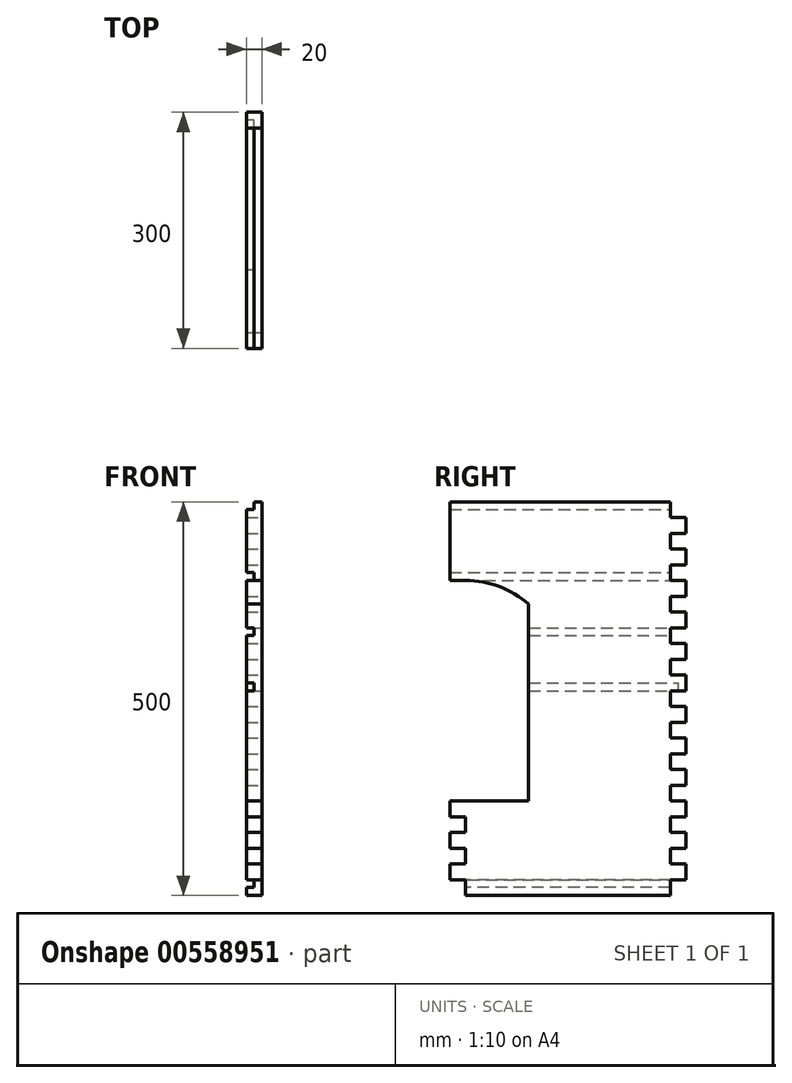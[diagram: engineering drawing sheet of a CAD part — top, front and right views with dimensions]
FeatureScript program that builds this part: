
annotation { "Feature Type Name" : "Feature", "Feature Type Description" : "" }
export const myFeature = defineFeature(function(context is Context, id is Id, definition is map)
    precondition{}
    {
        {
            var Q0;
            Q0=qCreatedBy(makeId("Right.planeOp"),FACE);
            var sketch = newSketch(context, id + "F0", { "sketchPlane" : qUnion([Q0])});
            skLineSegment(sketch, "E0.bottom", {"start": v(150, -250) * mm, "end": v(-150, -250) * mm});
            skLineSegment(sketch, "E0.left", {"start": v(150, -250) * mm, "end": v(150, 250) * mm});
            skPoint(sketch, "E0.middle", {"position": v(0, 0) * mm});
            skLineSegment(sketch, "E1", {"start": v(-150, -250) * mm, "end": v(-150, -130) * mm});
            skLineSegment(sketch, "E2", {"start": v(150, 250) * mm, "end": v(-50, 250) * mm});
            skLineSegment(sketch, "E3", {"start": v(-50, 250) * mm, "end": v(-50, -130) * mm});
            skLineSegment(sketch, "E4", {"start": v(-150, -130) * mm, "end": v(-50, -130) * mm});
            skSolve(sketch);
        }
        {
            var Q0;
            Q0=makeQuery(id+"F0.imprint","IMPRINT",FACE,{"disambiguationData":[TD([[makeQuery(id+"F0.imprint","IMPRINT",EDGE,{"derivedFrom":sQuery(id+"F0.wireOp",EDGE,"E0.bottom")}),-1.0]])]});
            extrude(context, id + "F1", {"entities" : qUnion([Q0]), "depth" : 20 * mm, "offsetDistance" : 25 * mm});
        }
        {
            var Q0;
            Q0=makeQuery(id+"F1.opExtrude","CAP_FACE",FACE,{"disambiguationData":[OSD([sQuery(id+"F0.wireOp",EDGE,"E0.bottom"),sQuery(id+"F0.wireOp",EDGE,"E0.left"),sQuery(id+"F0.wireOp",EDGE,"E1"),sQuery(id+"F0.wireOp",EDGE,"E2"),sQuery(id+"F0.wireOp",EDGE,"E3"),sQuery(id+"F0.wireOp",EDGE,"E4")])],"isStart":false});
            var sketch = newSketch(context, id + "F2", { "sketchPlane" : qUnion([Q0])});
            skLineSegment(sketch, "E5", {"start": v(-50, 250) * mm, "end": v(-150, 250) * mm});
            skLineSegment(sketch, "E6", {"start": v(-150, 250) * mm, "end": v(-150, 150) * mm});
            skLineSegment(sketch, "E7", {"start": v(-50, 120) * mm, "end": v(-50, 250) * mm});
            skLineSegment(sketch, "E8", {"start": v(-150, 150) * mm, "end": v(-130, 150) * mm});
            skArc(sketch, "E9", {"start": v(-130, 150) * mm, "mid": v(-87.28, 142.25) * mm, "end": v(-50, 120) * mm});
            skSolve(sketch);
        }
        {
            var Q0;
            Q0=makeQuery(id+"F2.imprint","IMPRINT",FACE,{"disambiguationData":[TD([[makeQuery(id+"F2.imprint","IMPRINT",EDGE,{"derivedFrom":sQuery(id+"F2.wireOp",EDGE,"E5")}),1.0]])]});
            extrude(context, id + "F3", {"entities" : qUnion([Q0]), "operationType" : NewBodyOperationType.ADD, "oppositeDirection" : true, "depth" : 20 * mm, "offsetDistance" : 25 * mm});
        }
        {
            var Q0;
            Q0=makeQuery(id+"F3.boolean.opBoolean","MERGE",FACE,{"derivedFrom":[makeQuery(id+"F1.opExtrude","CAP_FACE",FACE,{"disambiguationData":[OSD([sQuery(id+"F0.wireOp",EDGE,"E0.bottom"),sQuery(id+"F0.wireOp",EDGE,"E0.left"),sQuery(id+"F0.wireOp",EDGE,"E1"),sQuery(id+"F0.wireOp",EDGE,"E2"),sQuery(id+"F0.wireOp",EDGE,"E3"),sQuery(id+"F0.wireOp",EDGE,"E4")])],"isStart":false}),makeQuery(id+"F3.opExtrude","CAP_FACE",FACE,{"disambiguationData":[OSD([sQuery(id+"F2.wireOp",EDGE,"E5"),sQuery(id+"F2.wireOp",EDGE,"E6"),sQuery(id+"F2.wireOp",EDGE,"E7"),sQuery(id+"F2.wireOp",EDGE,"E8"),sQuery(id+"F2.wireOp",EDGE,"E9")])],"isStart":true})]});
            var sketch = newSketch(context, id + "F4", { "sketchPlane" : qUnion([Q0])});
            skLineSegment(sketch, "E10.bottom", {"start": v(150, -210) * mm, "end": v(130, -210) * mm});
            skLineSegment(sketch, "E10.top", {"start": v(150, -190) * mm, "end": v(130, -190) * mm});
            skLineSegment(sketch, "E10.left", {"start": v(150, -210) * mm, "end": v(150, -190) * mm});
            skLineSegment(sketch, "E10.right", {"start": v(130, -210) * mm, "end": v(130, -190) * mm});
            skLineSegment(sketch, "E11.bottom", {"start": v(150, -170) * mm, "end": v(130, -170) * mm});
            skLineSegment(sketch, "E11.top", {"start": v(150, -150) * mm, "end": v(130, -150) * mm});
            skLineSegment(sketch, "E11.left", {"start": v(150, -170) * mm, "end": v(150, -150) * mm});
            skLineSegment(sketch, "E11.right", {"start": v(130, -170) * mm, "end": v(130, -150) * mm});
            skLineSegment(sketch, "E12.bottom", {"start": v(150, -130) * mm, "end": v(130, -130) * mm});
            skLineSegment(sketch, "E12.top", {"start": v(150, -110) * mm, "end": v(130, -110) * mm});
            skLineSegment(sketch, "E12.left", {"start": v(150, -130) * mm, "end": v(150, -110) * mm});
            skLineSegment(sketch, "E12.right", {"start": v(130, -130) * mm, "end": v(130, -110) * mm});
            skLineSegment(sketch, "E13.bottom", {"start": v(150, -90) * mm, "end": v(130, -90) * mm});
            skLineSegment(sketch, "E13.top", {"start": v(150, -70) * mm, "end": v(130, -70) * mm});
            skLineSegment(sketch, "E13.left", {"start": v(150, -90) * mm, "end": v(150, -70) * mm});
            skLineSegment(sketch, "E13.right", {"start": v(130, -90) * mm, "end": v(130, -70) * mm});
            skLineSegment(sketch, "E14.bottom", {"start": v(150, -50) * mm, "end": v(130, -50) * mm});
            skLineSegment(sketch, "E14.top", {"start": v(150, -30) * mm, "end": v(130, -30) * mm});
            skLineSegment(sketch, "E14.left", {"start": v(150, -50) * mm, "end": v(150, -30) * mm});
            skLineSegment(sketch, "E14.right", {"start": v(130, -50) * mm, "end": v(130, -30) * mm});
            skLineSegment(sketch, "E15.bottom", {"start": v(150, -10) * mm, "end": v(130, -10) * mm});
            skLineSegment(sketch, "E15.top", {"start": v(150, 10) * mm, "end": v(130, 10) * mm});
            skLineSegment(sketch, "E15.left", {"start": v(150, -10) * mm, "end": v(150, 10) * mm});
            skLineSegment(sketch, "E15.right", {"start": v(130, -10) * mm, "end": v(130, 10) * mm});
            skLineSegment(sketch, "E16.bottom", {"start": v(150, 30) * mm, "end": v(130, 30) * mm});
            skLineSegment(sketch, "E16.top", {"start": v(150, 50) * mm, "end": v(130, 50) * mm});
            skLineSegment(sketch, "E16.left", {"start": v(150, 30) * mm, "end": v(150, 50) * mm});
            skLineSegment(sketch, "E16.right", {"start": v(130, 30) * mm, "end": v(130, 50) * mm});
            skLineSegment(sketch, "E17.bottom", {"start": v(150, 70) * mm, "end": v(130, 70) * mm});
            skLineSegment(sketch, "E17.top", {"start": v(150, 90) * mm, "end": v(130, 90) * mm});
            skLineSegment(sketch, "E17.left", {"start": v(150, 70) * mm, "end": v(150, 90) * mm});
            skLineSegment(sketch, "E17.right", {"start": v(130, 70) * mm, "end": v(130, 90) * mm});
            skLineSegment(sketch, "E18.bottom", {"start": v(150, 110) * mm, "end": v(130, 110) * mm});
            skLineSegment(sketch, "E18.top", {"start": v(150, 130) * mm, "end": v(130, 130) * mm});
            skLineSegment(sketch, "E18.left", {"start": v(150, 110) * mm, "end": v(150, 130) * mm});
            skLineSegment(sketch, "E18.right", {"start": v(130, 110) * mm, "end": v(130, 130) * mm});
            skLineSegment(sketch, "E19.bottom", {"start": v(150, 150) * mm, "end": v(130, 150) * mm});
            skLineSegment(sketch, "E19.top", {"start": v(150, 170) * mm, "end": v(130, 170) * mm});
            skLineSegment(sketch, "E19.left", {"start": v(150, 150) * mm, "end": v(150, 170) * mm});
            skLineSegment(sketch, "E19.right", {"start": v(130, 150) * mm, "end": v(130, 170) * mm});
            skLineSegment(sketch, "E20.bottom", {"start": v(150, 190) * mm, "end": v(130, 190) * mm});
            skLineSegment(sketch, "E20.top", {"start": v(150, 210) * mm, "end": v(130, 210) * mm});
            skLineSegment(sketch, "E20.left", {"start": v(150, 190) * mm, "end": v(150, 210) * mm});
            skLineSegment(sketch, "E20.right", {"start": v(130, 190) * mm, "end": v(130, 210) * mm});
            skLineSegment(sketch, "E21.bottom", {"start": v(150, 230) * mm, "end": v(130, 230) * mm});
            skLineSegment(sketch, "E21.top", {"start": v(150, 250) * mm, "end": v(130, 250) * mm});
            skLineSegment(sketch, "E21.left", {"start": v(150, 230) * mm, "end": v(150, 250) * mm});
            skLineSegment(sketch, "E21.right", {"start": v(130, 230) * mm, "end": v(130, 250) * mm});
            skLineSegment(sketch, "E22.bottom", {"start": v(150, -230) * mm, "end": v(130, -230) * mm});
            skLineSegment(sketch, "E22.top", {"start": v(150, -250) * mm, "end": v(130, -250) * mm});
            skLineSegment(sketch, "E22.left", {"start": v(150, -230) * mm, "end": v(150, -250) * mm});
            skLineSegment(sketch, "E22.right", {"start": v(130, -230) * mm, "end": v(130, -250) * mm});
            skSolve(sketch);
        }
        {
            var Q0;
            Q0=qSketchRegion(id+"F4",true);
            extrude(context, id + "F5", {"entities" : qUnion([Q0]), "operationType" : NewBodyOperationType.REMOVE, "endBound" : BoundingType.UP_TO_NEXT, "oppositeDirection" : true, "depth" : 25 * mm, "offsetDistance" : 25 * mm});
        }
        {
            var Q0;
            Q0=makeQuery(id+"F3.boolean.opBoolean","MERGE",FACE,{"derivedFrom":[makeQuery(id+"F1.opExtrude","CAP_FACE",FACE,{"disambiguationData":[OSD([sQuery(id+"F0.wireOp",EDGE,"E0.bottom"),sQuery(id+"F0.wireOp",EDGE,"E0.left"),sQuery(id+"F0.wireOp",EDGE,"E1"),sQuery(id+"F0.wireOp",EDGE,"E2"),sQuery(id+"F0.wireOp",EDGE,"E3"),sQuery(id+"F0.wireOp",EDGE,"E4")])],"isStart":false}),makeQuery(id+"F3.opExtrude","CAP_FACE",FACE,{"disambiguationData":[OSD([sQuery(id+"F2.wireOp",EDGE,"E5"),sQuery(id+"F2.wireOp",EDGE,"E6"),sQuery(id+"F2.wireOp",EDGE,"E7"),sQuery(id+"F2.wireOp",EDGE,"E8"),sQuery(id+"F2.wireOp",EDGE,"E9")])],"isStart":true})]});
            var sketch = newSketch(context, id + "F6", { "sketchPlane" : qUnion([Q0])});
            skLineSegment(sketch, "E23.bottom", {"start": v(-150, -210) * mm, "end": v(-130, -210) * mm});
            skLineSegment(sketch, "E23.top", {"start": v(-150, -190) * mm, "end": v(-130, -190) * mm});
            skLineSegment(sketch, "E23.left", {"start": v(-150, -210) * mm, "end": v(-150, -190) * mm});
            skLineSegment(sketch, "E23.right", {"start": v(-130, -210) * mm, "end": v(-130, -190) * mm});
            skLineSegment(sketch, "E24.bottom", {"start": v(-150, -170) * mm, "end": v(-130, -170) * mm});
            skLineSegment(sketch, "E24.top", {"start": v(-150, -150) * mm, "end": v(-130, -150) * mm});
            skLineSegment(sketch, "E24.left", {"start": v(-150, -170) * mm, "end": v(-150, -150) * mm});
            skLineSegment(sketch, "E24.right", {"start": v(-130, -170) * mm, "end": v(-130, -150) * mm});
            skLineSegment(sketch, "E25.bottom", {"start": v(-150, -250) * mm, "end": v(-130, -250) * mm});
            skLineSegment(sketch, "E25.top", {"start": v(-150, -230) * mm, "end": v(-130, -230) * mm});
            skLineSegment(sketch, "E25.left", {"start": v(-150, -250) * mm, "end": v(-150, -230) * mm});
            skLineSegment(sketch, "E25.right", {"start": v(-130, -250) * mm, "end": v(-130, -230) * mm});
            skSolve(sketch);
        }
        {
            var Q0;
            Q0=qSketchRegion(id+"F6",true);
            extrude(context, id + "F7", {"entities" : qUnion([Q0]), "operationType" : NewBodyOperationType.REMOVE, "endBound" : BoundingType.UP_TO_NEXT, "oppositeDirection" : true, "depth" : 25 * mm, "offsetDistance" : 25 * mm});
        }
        {
            var Q0;
            Q0=makeQuery(id+"F3.boolean.opBoolean","MERGE",FACE,{"derivedFrom":[makeQuery(id+"F1.opExtrude","CAP_FACE",FACE,{"disambiguationData":[OSD([sQuery(id+"F0.wireOp",EDGE,"E0.bottom"),sQuery(id+"F0.wireOp",EDGE,"E0.left"),sQuery(id+"F0.wireOp",EDGE,"E1"),sQuery(id+"F0.wireOp",EDGE,"E2"),sQuery(id+"F0.wireOp",EDGE,"E3"),sQuery(id+"F0.wireOp",EDGE,"E4")])],"isStart":true}),makeQuery(id+"F3.opExtrude","CAP_FACE",FACE,{"disambiguationData":[OSD([sQuery(id+"F2.wireOp",EDGE,"E5"),sQuery(id+"F2.wireOp",EDGE,"E6"),sQuery(id+"F2.wireOp",EDGE,"E7"),sQuery(id+"F2.wireOp",EDGE,"E8"),sQuery(id+"F2.wireOp",EDGE,"E9")])],"isStart":false})]});
            var sketch = newSketch(context, id + "F8", { "sketchPlane" : qUnion([Q0])});
            skLineSegment(sketch, "E26.bottom", {"start": v(-130, -230) * mm, "end": v(130, -230) * mm});
            skLineSegment(sketch, "E26.top", {"start": v(-130, -240) * mm, "end": v(130, -240) * mm});
            skLineSegment(sketch, "E26.left", {"start": v(-130, -230) * mm, "end": v(-130, -240) * mm});
            skLineSegment(sketch, "E26.right", {"start": v(130, -230) * mm, "end": v(130, -240) * mm});
            skSolve(sketch);
        }
        {
            var Q0;
            Q0 = qSketchRegion(id + "F8", true);
            extrude(context, id + "F9", {"entities" : qUnion([Q0]), "operationType" : NewBodyOperationType.REMOVE, "oppositeDirection" : true, "depth" : 10 * mm, "offsetDistance" : 25 * mm});
        }
        {
            var Q0;
            {var subQ0=sQuery(id+"F0.wireOp",EDGE,"E0.left");var subQ1=sQuery(id+"F2.wireOp",EDGE,"E5");var subQ2=sQuery(id+"F0.wireOp",EDGE,"E1");var subQ3=sQuery(id+"F2.wireOp",EDGE,"E9");var subQ4=sQuery(id+"F0.wireOp",EDGE,"E4");var subQ5=sQuery(id+"F2.wireOp",EDGE,"E6");var subQ6=sQuery(id+"F0.wireOp",EDGE,"E2");var subQ7=sQuery(id+"F2.wireOp",EDGE,"E8");var subQ8=sQuery(id+"F0.wireOp",EDGE,"E3");Q0=makeQuery(id+"F9.boolean.opBoolean","SPLIT",FACE,{"disambiguationData":[TD([makeQuery(id+"F1.opExtrude","SWEPT_FACE",FACE,{"disambiguationData":[OSD([subQ0])]})])],"derivedFrom":makeQuery(id+"F3.boolean.opBoolean","MERGE",FACE,{"derivedFrom":[makeQuery(id+"F1.opExtrude","CAP_FACE",FACE,{"disambiguationData":[OSD([sQuery(id+"F0.wireOp",EDGE,"E0.bottom"),subQ0,subQ2,subQ6,subQ8,subQ4])],"isStart":true}),makeQuery(id+"F3.opExtrude","CAP_FACE",FACE,{"disambiguationData":[OSD([subQ1,subQ5,sQuery(id+"F2.wireOp",EDGE,"E7"),subQ7,subQ3])],"isStart":false})]})});}
            var sketch = newSketch(context, id + "F10", { "sketchPlane" : qUnion([Q0])});
            skLineSegment(sketch, "E27.bottom", {"start": v(150, 240) * mm, "end": v(-150, 240) * mm});
            skLineSegment(sketch, "E27.top", {"start": v(150, 250) * mm, "end": v(-150, 250) * mm});
            skLineSegment(sketch, "E27.left", {"start": v(150, 240) * mm, "end": v(150, 250) * mm});
            skLineSegment(sketch, "E27.right", {"start": v(-150, 240) * mm, "end": v(-150, 250) * mm});
            skPoint(sketch, "E27.middle", {"position": v(0, 245) * mm});
            skLineSegment(sketch, "E28.bottom", {"start": v(150, 150) * mm, "end": v(-150, 150) * mm});
            skLineSegment(sketch, "E28.top", {"start": v(150, 160) * mm, "end": v(-150, 160) * mm});
            skLineSegment(sketch, "E28.left", {"start": v(150, 150) * mm, "end": v(150, 160) * mm});
            skLineSegment(sketch, "E28.right", {"start": v(-150, 150) * mm, "end": v(-150, 160) * mm});
            skPoint(sketch, "E28.middle", {"position": v(0, 155) * mm});
            skLineSegment(sketch, "E29.bottom", {"start": v(140, 80) * mm, "end": v(-140, 80) * mm});
            skLineSegment(sketch, "E29.top", {"start": v(140, 90) * mm, "end": v(-140, 90) * mm});
            skLineSegment(sketch, "E29.left", {"start": v(140, 80) * mm, "end": v(140, 90) * mm});
            skLineSegment(sketch, "E29.right", {"start": v(-140, 80) * mm, "end": v(-140, 90) * mm});
            skPoint(sketch, "E29.middle", {"position": v(0, 85) * mm});
            skLineSegment(sketch, "E30.bottom", {"start": v(140, 10) * mm, "end": v(-140, 10) * mm});
            skLineSegment(sketch, "E30.top", {"start": v(140, 20) * mm, "end": v(-140, 20) * mm});
            skLineSegment(sketch, "E30.left", {"start": v(140, 10) * mm, "end": v(140, 20) * mm});
            skLineSegment(sketch, "E30.right", {"start": v(-140, 10) * mm, "end": v(-140, 20) * mm});
            skPoint(sketch, "E30.middle", {"position": v(0, 15) * mm});
            skSolve(sketch);
        }
        {
            var Q0;
            Q0 = qSketchRegion(id + "F10", true);
            extrude(context, id + "F11", {"entities" : qUnion([Q0]), "operationType" : NewBodyOperationType.REMOVE, "oppositeDirection" : true, "depth" : 10 * mm, "offsetDistance" : 25 * mm});
        }
    });
